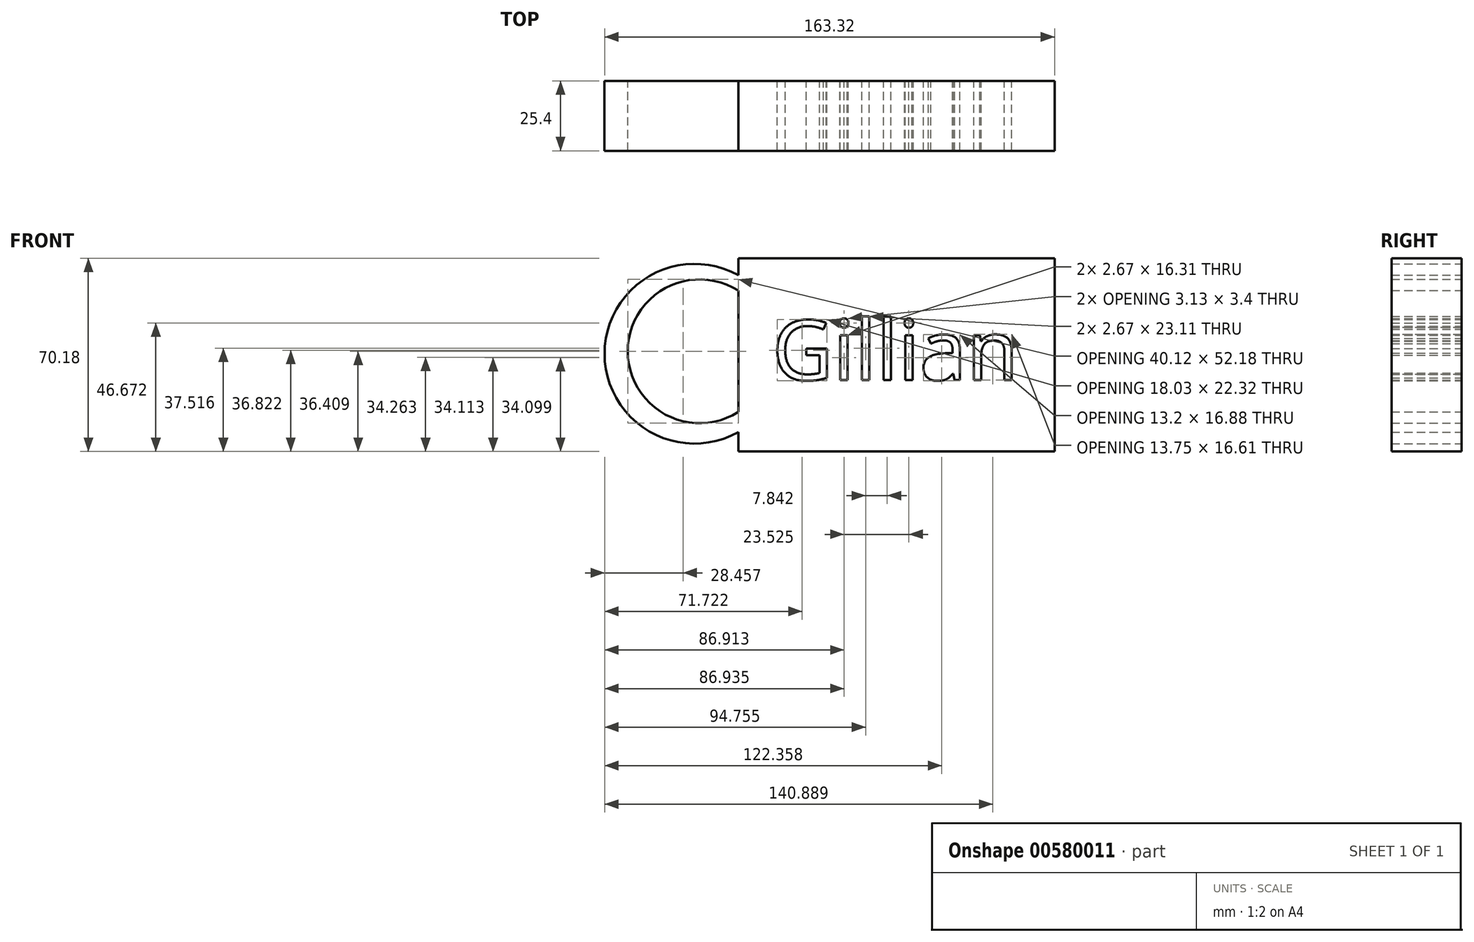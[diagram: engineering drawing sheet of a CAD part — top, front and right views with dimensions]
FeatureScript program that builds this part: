
annotation { "Feature Type Name" : "Feature", "Feature Type Description" : "" }
export const myFeature = defineFeature(function(context is Context, id is Id, definition is map)
    precondition{}
    {
        {
            var Q0;
            Q0=qCreatedBy(makeId("Front.planeOp"),FACE);
            var sketch = newSketch(context, id + "F0", { "sketchPlane" : qUnion([Q0])});
            skLineSegment(sketch, "E0.bottom", {"start": v(-42.57, 36.56) * mm, "end": v(72.23, 36.56) * mm});
            skLineSegment(sketch, "E0.top", {"start": v(-42.57, -33.62) * mm, "end": v(72.23, -33.62) * mm});
            skLineSegment(sketch, "E0.left", {"start": v(-42.57, 36.56) * mm, "end": v(-42.57, -33.62) * mm});
            skLineSegment(sketch, "E0.right", {"start": v(72.23, 36.56) * mm, "end": v(72.23, -33.62) * mm});
            skArc(sketch, "E1", {"start": v(-42.57, 30.39) * mm, "mid": v(-91.1, 1.9) * mm, "end": v(-42.57, -26.57) * mm});
            skArc(sketch, "E2", {"start": v(-42.57, 24.81) * mm, "mid": v(-82.7, 2.79) * mm, "end": v(-42.57, -19.23) * mm});
            skLineSegment(sketch, "E3.0", {"start": v(-42.57, 30.2) * mm, "end": v(72.23, 30.2) * mm});
            skLineSegment(sketch, "E4.0", {"start": v(-42.57, -27.27) * mm, "end": v(72.23, -27.27) * mm});
            skLineSegment(sketch, "E5.0", {"start": v(-36.22, 36.56) * mm, "end": v(-36.22, -33.62) * mm});
            skLineSegment(sketch, "E6.0", {"start": v(65.88, 36.56) * mm, "end": v(65.88, -33.62) * mm});
            skText(sketch, "E7", { "text": "Gillian", "fontName": "NotoSans-Regular.ttf"});
            const initialGuessF0  = {"E7": [-0.03024, -0.00766, 1, 0, 0.0219]};
            skSetInitialGuess(sketch, initialGuessF0);
            skSolve(sketch);
        }
        {
            var Q0;
            Q0 = qSketchRegion(id + "F0", true);
            var Q1;
            Q1=makeQuery(id+"F0.imprint","IMPRINT",FACE,{"disambiguationData":[TD([[makeQuery(id+"F0.imprint","IMPRINT",EDGE,{"derivedFrom":sQuery(id+"F0.wireOp",EDGE,"E7.sketch_text.stroke-0")}),1.0]])]});
            extrude(context, id + "F1", {"entities" : qUnion([Q0, Q1]), "depth" : 25.4 * mm, "offsetDistance" : 25.4 * mm});
        }
    });
